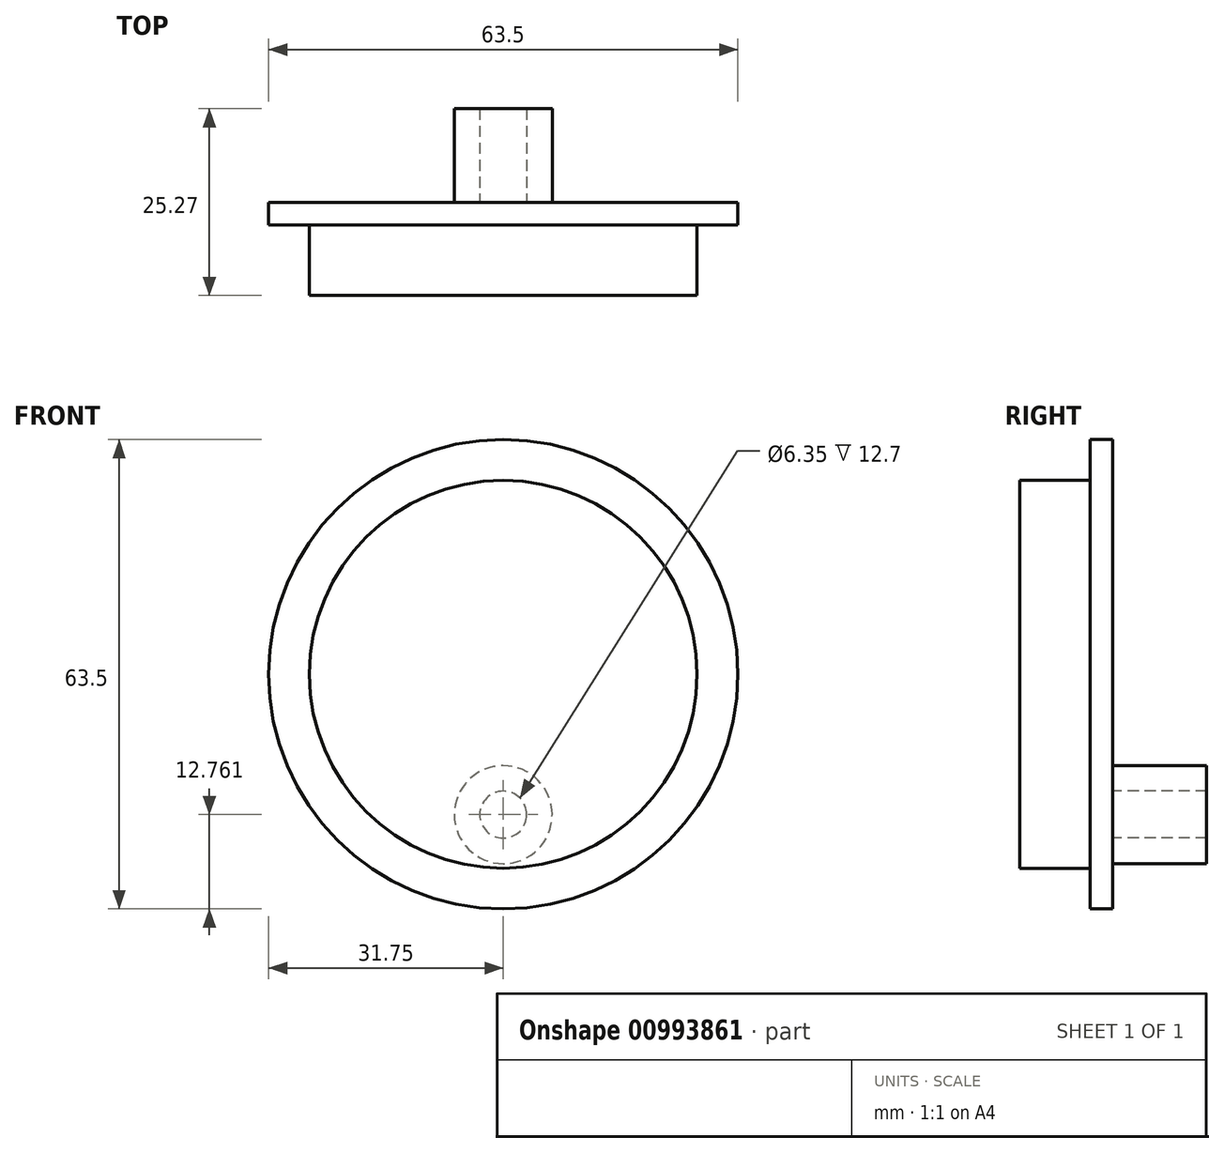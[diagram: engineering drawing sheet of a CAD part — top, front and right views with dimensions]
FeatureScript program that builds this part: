
annotation { "Feature Type Name" : "Feature", "Feature Type Description" : "" }
export const myFeature = defineFeature(function(context is Context, id is Id, definition is map)
    precondition{}
    {
        {
            var Q0;
            Q0=qCreatedBy(makeId("Front.planeOp"),FACE);
            var sketch = newSketch(context, id + "F0", { "sketchPlane" : qUnion([Q0])});
            skCircle(sketch, "E0", {"center": v(0, 0) * mm, "radius": 31.75 * mm});
            skSolve(sketch);
        }
        {
            var Q0;
            Q0 = qSketchRegion(id + "F0", true);
            extrude(context, id + "F1", {"entities" : qUnion([Q0]), "depth" : 3.05 * mm, "offsetDistance" : 25.4 * mm});
        }
        {
            var Q0;
            Q0=makeQuery(id+"F1.opExtrude","CAP_FACE",FACE,{"disambiguationData":[OSD([sQuery(id+"F0.wireOp",EDGE,"E0")])],"isStart":false});
            var sketch = newSketch(context, id + "F2", { "sketchPlane" : qUnion([Q0])});
            skCircle(sketch, "E1", {"center": v(0, 0) * mm, "radius": 26.24 * mm});
            skSolve(sketch);
        }
        {
            var Q0;
            Q0 = qSketchRegion(id + "F2", true);
            extrude(context, id + "F3", {"entities" : qUnion([Q0]), "operationType" : NewBodyOperationType.ADD, "depth" : 9.52 * mm, "offsetDistance" : 25.4 * mm});
        }
        {
            var Q0;
            Q0=makeQuery(id+"F1.opExtrude","CAP_FACE",FACE,{"disambiguationData":[OSD([sQuery(id+"F0.wireOp",EDGE,"E0")])],"isStart":true});
            var sketch = newSketch(context, id + "F4", { "sketchPlane" : qUnion([Q0])});
            skCircle(sketch, "E2", {"center": v(0, -18.99) * mm, "radius": 6.63 * mm});
            skCircle(sketch, "E3", {"center": v(0, -18.99) * mm, "radius": 3.18 * mm});
            skSolve(sketch);
        }
        {
            var Q0;
            Q0 = qSketchRegion(id + "F4", true);
            extrude(context, id + "F5", {"entities" : qUnion([Q0]), "operationType" : NewBodyOperationType.ADD, "depth" : 12.7 * mm, "offsetDistance" : 25.4 * mm});
        }
    });
